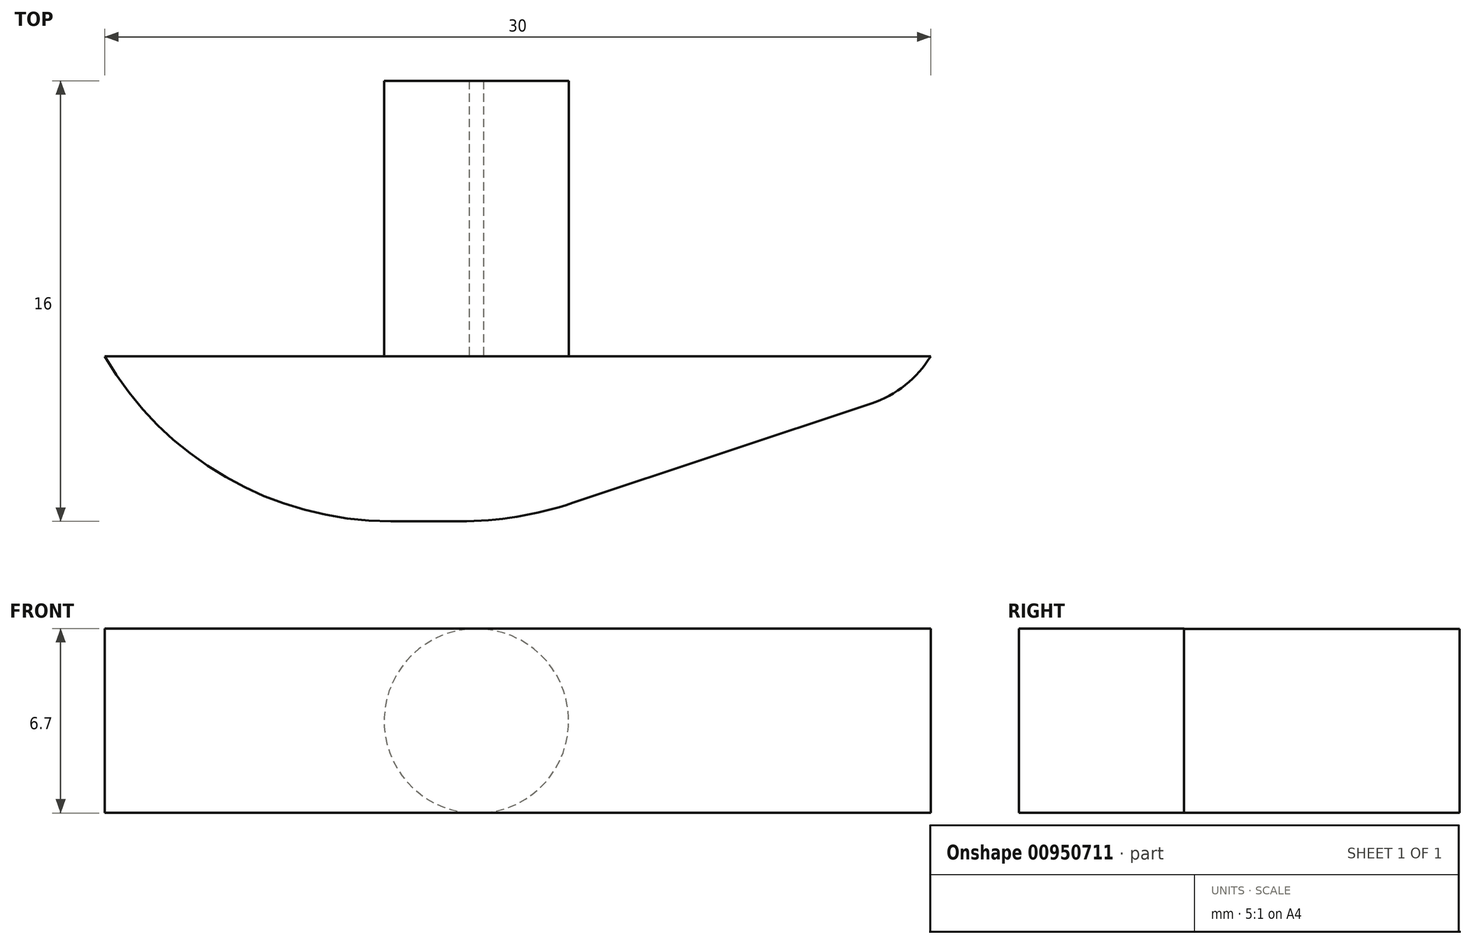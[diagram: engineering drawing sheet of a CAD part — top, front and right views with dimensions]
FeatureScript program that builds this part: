
annotation { "Feature Type Name" : "Feature", "Feature Type Description" : "" }
export const myFeature = defineFeature(function(context is Context, id is Id, definition is map)
    precondition{}
    {
        {
            var Q0;
            Q0=qCreatedBy(makeId("Front.planeOp"),FACE);
            var sketch = newSketch(context, id + "F0", { "sketchPlane" : qUnion([Q0])});
            skLineSegment(sketch, "E0.bottom", {"start": v(-14.7, 3.35) * mm, "end": v(15.3, 3.35) * mm});
            skLineSegment(sketch, "E0.top", {"start": v(-14.7, -3.35) * mm, "end": v(15.3, -3.35) * mm});
            skLineSegment(sketch, "E0.left", {"start": v(-14.7, 3.35) * mm, "end": v(-14.7, -3.35) * mm});
            skLineSegment(sketch, "E0.right", {"start": v(15.3, 3.35) * mm, "end": v(15.3, -3.35) * mm});
            skCircle(sketch, "E1", {"center": v(-1.2, 0) * mm, "radius": 3.35 * mm});
            skSolve(sketch);
        }
        {
            var Q0;
            {var subQ0=sQuery(id+"F0.wireOp",EDGE,"E1");var subQ1=sQuery(id+"F0.wireOp",EDGE,"E0.top");var subQ2=makeQuery(id+"F0.imprint","INTERSECT",VERTEX,{"disambiguationData":[OD(0.0)],"derivedFrom":[subQ1,subQ0]});Q0=makeQuery(id+"F0.imprint","IMPRINT",FACE,{"disambiguationData":[TD([[makeQuery(id+"F0.imprint","IMPRINT",EDGE,{"disambiguationData":[TD([[subQ2,-1.0]])],"derivedFrom":subQ1}),1.0]])]});}
            extrude(context, id + "F1", {"entities" : qUnion([Q0]), "oppositeDirection" : true, "depth" : 10 * mm, "offsetDistance" : 25 * mm});
        }
        {
            var Q0;
            Q0=makeQuery(id+"F0.imprint","IMPRINT",FACE,{"disambiguationData":[TD([[makeQuery(id+"F0.imprint","IMPRINT",EDGE,{"derivedFrom":sQuery(id+"F0.wireOp",EDGE,"E0.bottom")}),-1.0]])]});
            var Q1;
            {var subQ0=sQuery(id+"F0.wireOp",EDGE,"E1");var subQ1=sQuery(id+"F0.wireOp",EDGE,"E0.top");var subQ2=makeQuery(id+"F0.imprint","INTERSECT",VERTEX,{"disambiguationData":[OD(0.0)],"derivedFrom":[subQ1,subQ0]});Q1=makeQuery(id+"F0.imprint","IMPRINT",FACE,{"disambiguationData":[TD([[makeQuery(id+"F0.imprint","IMPRINT",EDGE,{"disambiguationData":[TD([[subQ2,-1.0]])],"derivedFrom":subQ1}),1.0]])]});}
            extrude(context, id + "F2", {"entities" : qUnion([Q0, Q1]), "operationType" : NewBodyOperationType.ADD, "depth" : 6 * mm, "offsetDistance" : 25 * mm});
        }
        {
            var Q0;
            Q0=makeQuery(id+"F2.opExtrude","CAP_EDGE",EDGE,{"disambiguationData":[OSD([sQuery(id+"F0.wireOp",EDGE,"E0.right")])],"isStart":false});
            chamfer(context, id + "F3", {"entities" : qUnion([Q0]), "chamferType" : ChamferType.TWO_OFFSETS, "width1" : 5 * mm, "oppositeDirection" : false, "width2" : 15 * mm, "tangentPropagation" : true});
        }
        {
            var Q0;
            Q0=makeQuery(id+"F2.opExtrude","CAP_EDGE",EDGE,{"disambiguationData":[OSD([sQuery(id+"F0.wireOp",EDGE,"E0.left")])],"isStart":false});
            fillet(context, id + "F4", {"entities" : qUnion([Q0]), "radius" : 12 * mm, "tangentPropagation" : true, "allowEdgeOverflow" : false});
        }
        {
            var Q0;
            {var subQ0=sQuery(id+"F0.wireOp",EDGE,"E0.right");Q0=makeQuery(id+"F3.opChamfer","BLEND_EDGE",EDGE,{"blendedFrom":[makeQuery(id+"F2.opExtrude","CAP_EDGE",EDGE,{"disambiguationData":[OSD([subQ0])],"isStart":false}),makeQuery(id+"F2.opExtrude","CAP_FACE",FACE,{"disambiguationData":[OSD([sQuery(id+"F0.wireOp",EDGE,"E0.bottom"),sQuery(id+"F0.wireOp",EDGE,"E0.top"),sQuery(id+"F0.wireOp",EDGE,"E0.left"),subQ0])],"isStart":false})],"blendedInto":[makeQuery(id+"F2.opExtrude","CAP_FACE",FACE,{"disambiguationData":[OSD([sQuery(id+"F0.wireOp",EDGE,"E0.bottom"),sQuery(id+"F0.wireOp",EDGE,"E0.top"),sQuery(id+"F0.wireOp",EDGE,"E0.left"),subQ0])],"isStart":false})]});}
            fillet(context, id + "F5", {"entities" : qUnion([Q0]), "radius" : 13 * mm, "tangentPropagation" : true, "allowEdgeOverflow" : false});
        }
        {
            var Q0;
            {var subQ0=sQuery(id+"F0.wireOp",EDGE,"E0.right");Q0=makeQuery(id+"F3.opChamfer","BLEND_EDGE",EDGE,{"blendedFrom":[makeQuery(id+"F2.opExtrude","CAP_EDGE",EDGE,{"disambiguationData":[OSD([subQ0])],"isStart":false}),makeQuery(id+"F2.opExtrude","SWEPT_FACE",FACE,{"disambiguationData":[OSD([subQ0])]})],"blendedInto":[makeQuery(id+"F2.opExtrude","SWEPT_FACE",FACE,{"disambiguationData":[OSD([subQ0])]})]});}
            fillet(context, id + "F6", {"entities" : qUnion([Q0]), "radius" : 4 * mm, "tangentPropagation" : true, "allowEdgeOverflow" : false});
        }
    });
